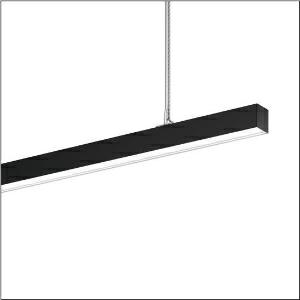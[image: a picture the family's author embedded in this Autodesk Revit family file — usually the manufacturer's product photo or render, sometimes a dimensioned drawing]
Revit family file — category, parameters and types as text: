
# Revit family: silica_r__21_51mx33da47bb_630a
name_source: partatom
category: Lighting Fixtures
units: mm (PartAtom-declared; Revit-internal decimal feet)

## family parameters
Cut with Voids When Loaded = No
Host = Face
Light Source = No
Part Type = Normal
Room Calculation Point = No
Round Connector Dimension = Use Diameter
Shared = No

## types (1)
- --- (1 x LED, 5910 lm, 38.4 W, 4000K)
    Apparent Load = 38 VA
    CIE Flux Codes = 78 96 99 55 100
    Color Rendering = 80
    Color Temperature = 4000K
    Default Elevation = 1800 mm
    Description = Silica® 21, office luminaire, primary optical cover: prismatic diffuser, of PMMA, CAT 2 (L<= 3000cd/m²), light emission: direct/indirect distribution, primary light characteristic: symmetric, installation type: suspended mounting, LED, rated luminous flux: 5.910lm, luminous efficacy: 154lm/W, light colour: 840, colour temperature: 4000K, with terminal, 3+2-pole, max. 2.5mm², mains connection: 220..240V, AC, 50/60Hz, rated input power: 38.4W, luminaire housing, of aluminium, jet black (RAL 9005), length: 1.204mm, width: 53mm, height: 53mm, protection rating (complete): IP20, insulation class (complete): insulation class I (protective earthing), certification: CE, permissible operating ambient temperature: 0..+35°C, standard: EN 50419, packaging unit: 1 piece
    Height = 53 mm
    Lamp = 1 x LED
    Lamp Light Flux = 5910 lm
    Lamp Power = 38.4 W
    Lamp count = 1
    Length = 1204 mm
    Luminous efficacy = 154 lm/W
    Manufacturer = Siteco
    ModVariant = No
    Model = 51MX33DA47BB
    Mounting Place = Ceiling
    Mounting Type = Pendant
    Number of Poles = 1
    OnlyDefault = Yes
    Power Factor = 1
    Product Name = Silica® 21
    Product group = office luminaire | ceiling pendant
    ProductGroupID = 902
    Protection Class = Protection class I
    Protection Degree = IP 20
    RLX_Detail_Level = 1
    RLX_Emergency_Light_Flux = 0 lm
    RLX_Emergency_Type = 0
    RLX_Emergency_Type_DB = No
    RlxData = <blob elided: 25841 chars, md5=f50dbf86>
    Socket = socket
    Standby Power = 0 W
    System Light Flux = 5910 lm
    System Power = 38 W
    Type Comments = factory setting: luminous flux: 100 % | dim-lin: 254 | 323 mA
    Type Image = l_1297744.jpg
    URL = http://relux.com
    VarID = @adj_049113
    Voltage = 0 V
    Weight = 0.00 kg
    Width = 53 mm

## geometry (parser evidence)
native form markers: Blend x4, Sweep x14
no freeform markers — native parametric forms only
